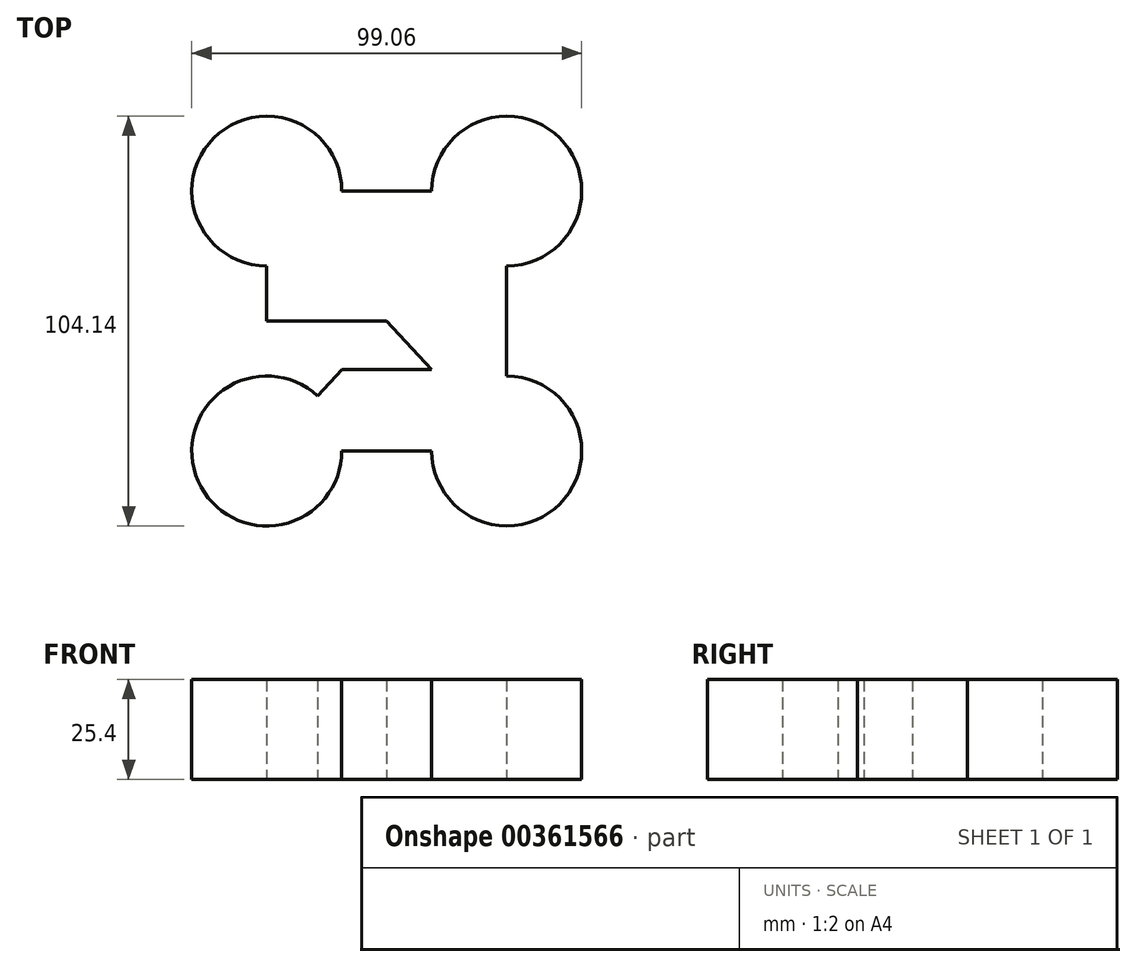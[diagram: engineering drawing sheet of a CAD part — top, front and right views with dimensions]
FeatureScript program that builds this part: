
annotation { "Feature Type Name" : "Feature", "Feature Type Description" : "" }
export const myFeature = defineFeature(function(context is Context, id is Id, definition is map)
    precondition{}
    {
        {
            var Q0;
            Q0=qCreatedBy(makeId("Top.planeOp"),FACE);
            var sketch = newSketch(context, id + "F0", { "sketchPlane" : qUnion([Q0])});
            skLineSegment(sketch, "E0", {"start": v(-76.2, 0) * mm, "end": v(76.2, 0) * mm});
            skPoint(sketch, "E1", {"position": v(-30.48, 0) * mm});
            skLineSegment(sketch, "E2", {"start": v(-76.2, 33.02) * mm, "end": v(76.2, 33.02) * mm});
            skPoint(sketch, "E3", {"position": v(-30.48, 33.02) * mm});
            skLineSegment(sketch, "E4", {"start": v(-30.48, 33.02) * mm, "end": v(0, 0) * mm});
            skPoint(sketch, "E5", {"position": v(30.48, 0) * mm});
            skPoint(sketch, "E6", {"position": v(0, 0) * mm});
            skPoint(sketch, "E7", {"position": v(30.48, 33.02) * mm});
            skLineSegment(sketch, "E8", {"start": v(0, 0) * mm, "end": v(30.48, 33.02) * mm});
            skLineSegment(sketch, "E9", {"start": v(-30.48, 0) * mm, "end": v(-30.48, -33.02) * mm});
            skLineSegment(sketch, "E10", {"start": v(-30.48, -33.02) * mm, "end": v(0, 0) * mm});
            skLineSegment(sketch, "E11", {"start": v(0, 0) * mm, "end": v(30.48, -33.02) * mm});
            skLineSegment(sketch, "E12", {"start": v(30.48, -33.02) * mm, "end": v(30.48, 33.02) * mm});
            skLineSegment(sketch, "E13", {"start": v(30.48, -33.02) * mm, "end": v(-30.48, -33.02) * mm});
            skLineSegment(sketch, "E14", {"start": v(-30.48, 0) * mm, "end": v(-30.48, 33.02) * mm});
            skCircle(sketch, "E15", {"center": v(-30.48, 33.02) * mm, "radius": 19.05 * mm});
            skCircle(sketch, "E16", {"center": v(30.48, 33.02) * mm, "radius": 19.05 * mm});
            skCircle(sketch, "E17", {"center": v(-30.48, -33.02) * mm, "radius": 19.05 * mm});
            skCircle(sketch, "E18", {"center": v(30.48, -33.02) * mm, "radius": 19.05 * mm});
            skLineSegment(sketch, "E19.bottom", {"start": v(11.42, 12.37) * mm, "end": v(-11.42, 12.37) * mm});
            skLineSegment(sketch, "E19.top", {"start": v(11.42, -12.37) * mm, "end": v(-11.42, -12.37) * mm});
            skLineSegment(sketch, "E19.left", {"start": v(11.42, 12.37) * mm, "end": v(11.42, -12.37) * mm});
            skLineSegment(sketch, "E19.right", {"start": v(-11.42, 12.37) * mm, "end": v(-11.42, -12.37) * mm});
            skPoint(sketch, "E20", {"position": v(-17.56, 19.02) * mm});
            skPoint(sketch, "E21", {"position": v(17.56, 19.02) * mm});
            skPoint(sketch, "E22", {"position": v(-17.56, -19.02) * mm});
            skPoint(sketch, "E23", {"position": v(17.56, -19.02) * mm});
            skSolve(sketch);
        }
        {
            var Q0;
            {var subQ0=sQuery(id+"F0.wireOp",EDGE,"E4");Q0=makeQuery(id+"F0.imprint","IMPRINT",FACE,{"disambiguationData":[TD([[makeQuery(id+"F0.imprint","IMPRINT",EDGE,{"derivedFrom":subQ0}),1.0]])]});}
            var Q1;
            {var subQ2=sQuery(id+"F0.wireOp",EDGE,"E9");Q1=makeQuery(id+"F0.imprint","IMPRINT",FACE,{"disambiguationData":[TD([[makeQuery(id+"F0.imprint","IMPRINT",EDGE,{"derivedFrom":subQ2}),1.0]])]});}
            var Q2;
            {var subQ0=sQuery(id+"F0.wireOp",EDGE,"E4");Q2=makeQuery(id+"F0.imprint","IMPRINT",FACE,{"disambiguationData":[TD([[makeQuery(id+"F0.imprint","IMPRINT",EDGE,{"derivedFrom":subQ0}),-1.0]])]});}
            var Q3;
            {var subQ0=sQuery(id+"F0.wireOp",EDGE,"E8");Q3=makeQuery(id+"F0.imprint","IMPRINT",FACE,{"disambiguationData":[TD([[makeQuery(id+"F0.imprint","IMPRINT",EDGE,{"derivedFrom":subQ0}),-1.0]])]});}
            var Q4;
            {var subQ0=sQuery(id+"F0.wireOp",EDGE,"E11");Q4=makeQuery(id+"F0.imprint","IMPRINT",FACE,{"disambiguationData":[TD([[makeQuery(id+"F0.imprint","IMPRINT",EDGE,{"derivedFrom":subQ0}),1.0]])]});}
            var Q5;
            {var subQ0=sQuery(id+"F0.wireOp",EDGE,"E2");var subQ2=sQuery(id+"F0.wireOp",EDGE,"E15");var subQ3=makeQuery(id+"F0.imprint","INTERSECT",VERTEX,{"disambiguationData":[OD(0.0)],"derivedFrom":[subQ0,subQ2]});Q5=makeQuery(id+"F0.imprint","IMPRINT",FACE,{"disambiguationData":[TD([[makeQuery(id+"F0.imprint","IMPRINT",EDGE,{"disambiguationData":[TD([[subQ3,1.0]])],"derivedFrom":subQ2}),1.0]])]});}
            var Q6;
            {var subQ1=sQuery(id+"F0.wireOp",EDGE,"E2");var subQ3=sQuery(id+"F0.wireOp",EDGE,"E15");var subQ4=makeQuery(id+"F0.imprint","INTERSECT",VERTEX,{"disambiguationData":[OD(0.0)],"derivedFrom":[subQ1,subQ3]});Q6=makeQuery(id+"F0.imprint","IMPRINT",FACE,{"disambiguationData":[TD([[makeQuery(id+"F0.imprint","IMPRINT",EDGE,{"disambiguationData":[TD([[subQ4,-1.0]])],"derivedFrom":subQ3}),1.0]])]});}
            var Q7;
            {var subQ0=sQuery(id+"F0.wireOp",EDGE,"E2");var subQ2=sQuery(id+"F0.wireOp",EDGE,"E16");var subQ4=makeQuery(id+"F0.imprint","INTERSECT",VERTEX,{"disambiguationData":[OD(0.0)],"derivedFrom":[subQ0,subQ2]});Q7=makeQuery(id+"F0.imprint","IMPRINT",FACE,{"disambiguationData":[TD([[makeQuery(id+"F0.imprint","IMPRINT",EDGE,{"disambiguationData":[TD([[subQ4,-1.0]])],"derivedFrom":subQ2}),1.0]])]});}
            var Q8;
            {var subQ1=sQuery(id+"F0.wireOp",EDGE,"E2");var subQ3=sQuery(id+"F0.wireOp",EDGE,"E16");var subQ4=makeQuery(id+"F0.imprint","INTERSECT",VERTEX,{"disambiguationData":[OD(0.0)],"derivedFrom":[subQ1,subQ3]});Q8=makeQuery(id+"F0.imprint","IMPRINT",FACE,{"disambiguationData":[TD([[makeQuery(id+"F0.imprint","IMPRINT",EDGE,{"disambiguationData":[TD([[subQ4,1.0]])],"derivedFrom":subQ3}),1.0]])]});}
            var Q9;
            {var subQ1=sQuery(id+"F0.wireOp",EDGE,"E2");var subQ3=sQuery(id+"F0.wireOp",EDGE,"E16");var subQ4=makeQuery(id+"F0.imprint","INTERSECT",VERTEX,{"disambiguationData":[OD(1.0)],"derivedFrom":[subQ1,subQ3]});Q9=makeQuery(id+"F0.imprint","IMPRINT",FACE,{"disambiguationData":[TD([[makeQuery(id+"F0.imprint","IMPRINT",EDGE,{"disambiguationData":[TD([[subQ4,-1.0]])],"derivedFrom":subQ3}),1.0]])]});}
            var Q10;
            {var subQ1=sQuery(id+"F0.wireOp",EDGE,"E9");var subQ3=sQuery(id+"F0.wireOp",EDGE,"E17");var subQ4=makeQuery(id+"F0.imprint","INTERSECT",VERTEX,{"derivedFrom":[subQ1,subQ3]});Q10=makeQuery(id+"F0.imprint","IMPRINT",FACE,{"disambiguationData":[TD([[makeQuery(id+"F0.imprint","IMPRINT",EDGE,{"disambiguationData":[TD([[subQ4,-1.0]])],"derivedFrom":subQ3}),1.0]])]});}
            var Q11;
            {var subQ1=sQuery(id+"F0.wireOp",EDGE,"E12");var subQ3=sQuery(id+"F0.wireOp",EDGE,"E18");var subQ4=makeQuery(id+"F0.imprint","INTERSECT",VERTEX,{"derivedFrom":[subQ1,subQ3]});Q11=makeQuery(id+"F0.imprint","IMPRINT",FACE,{"disambiguationData":[TD([[makeQuery(id+"F0.imprint","IMPRINT",EDGE,{"disambiguationData":[TD([[subQ4,1.0]])],"derivedFrom":subQ3}),1.0]])]});}
            var Q12;
            {var subQ0=sQuery(id+"F0.wireOp",EDGE,"E13");var subQ3=sQuery(id+"F0.wireOp",EDGE,"E18");var subQ5=makeQuery(id+"F0.imprint","INTERSECT",VERTEX,{"derivedFrom":[subQ0,subQ3]});Q12=makeQuery(id+"F0.imprint","IMPRINT",FACE,{"disambiguationData":[TD([[makeQuery(id+"F0.imprint","IMPRINT",EDGE,{"disambiguationData":[TD([[subQ5,1.0]])],"derivedFrom":subQ3}),1.0]])]});}
            var Q13;
            {var subQ1=sQuery(id+"F0.wireOp",EDGE,"E10");var subQ3=sQuery(id+"F0.wireOp",EDGE,"E17");var subQ4=makeQuery(id+"F0.imprint","INTERSECT",VERTEX,{"derivedFrom":[subQ1,subQ3]});Q13=makeQuery(id+"F0.imprint","IMPRINT",FACE,{"disambiguationData":[TD([[makeQuery(id+"F0.imprint","IMPRINT",EDGE,{"disambiguationData":[TD([[subQ4,1.0]])],"derivedFrom":subQ3}),1.0]])]});}
            var Q14;
            {var subQ3=sQuery(id+"F0.wireOp",EDGE,"E18");var subQ5=sQuery(id+"F0.wireOp",EDGE,"E13");var subQ6=makeQuery(id+"F0.imprint","INTERSECT",VERTEX,{"derivedFrom":[subQ5,subQ3]});Q14=makeQuery(id+"F0.imprint","IMPRINT",FACE,{"disambiguationData":[TD([[makeQuery(id+"F0.imprint","IMPRINT",EDGE,{"disambiguationData":[TD([[subQ6,-1.0]])],"derivedFrom":subQ5}),-1.0]])]});}
            var Q15;
            {var subQ3=sQuery(id+"F0.wireOp",EDGE,"E14");var subQ5=sQuery(id+"F0.wireOp",EDGE,"E15");var subQ7=makeQuery(id+"F0.imprint","INTERSECT",VERTEX,{"derivedFrom":[subQ3,subQ5]});Q15=makeQuery(id+"F0.imprint","IMPRINT",FACE,{"disambiguationData":[TD([[makeQuery(id+"F0.imprint","IMPRINT",EDGE,{"disambiguationData":[TD([[subQ7,-1.0]])],"derivedFrom":subQ5}),-1.0]])]});}
            var Q16;
            {var subQ0=sQuery(id+"F0.wireOp",EDGE,"E15");var subQ1=sQuery(id+"F0.wireOp",EDGE,"E2");var subQ2=makeQuery(id+"F0.imprint","INTERSECT",VERTEX,{"disambiguationData":[OD(1.0)],"derivedFrom":[subQ1,subQ0]});Q16=makeQuery(id+"F0.imprint","IMPRINT",FACE,{"disambiguationData":[TD([[makeQuery(id+"F0.imprint","IMPRINT",EDGE,{"disambiguationData":[TD([[subQ2,-1.0]])],"derivedFrom":subQ1}),-1.0]])]});}
            var Q17;
            {var subQ1=sQuery(id+"F0.wireOp",EDGE,"E0");var subQ3=sQuery(id+"F0.wireOp",EDGE,"E12");var subQ4=makeQuery(id+"F0.imprint","INTERSECT",VERTEX,{"derivedFrom":[subQ1,subQ3]});Q17=makeQuery(id+"F0.imprint","IMPRINT",FACE,{"disambiguationData":[TD([[makeQuery(id+"F0.imprint","IMPRINT",EDGE,{"disambiguationData":[TD([[subQ4,-1.0]])],"derivedFrom":subQ3}),1.0]])]});}
            var Q18;
            {var subQ1=sQuery(id+"F0.wireOp",EDGE,"E0");var subQ3=sQuery(id+"F0.wireOp",EDGE,"E12");var subQ4=makeQuery(id+"F0.imprint","INTERSECT",VERTEX,{"derivedFrom":[subQ1,subQ3]});Q18=makeQuery(id+"F0.imprint","IMPRINT",FACE,{"disambiguationData":[TD([[makeQuery(id+"F0.imprint","IMPRINT",EDGE,{"disambiguationData":[TD([[subQ4,1.0]])],"derivedFrom":subQ3}),1.0]])]});}
            extrude(context, id + "F1", {"entities" : qUnion([Q0, Q1, Q2, Q3, Q4, Q5, Q6, Q7, Q8, Q9, Q10, Q11, Q12, Q13, Q14, Q15, Q16, Q17, Q18]), "depth" : 25.4 * mm});
        }
    });
